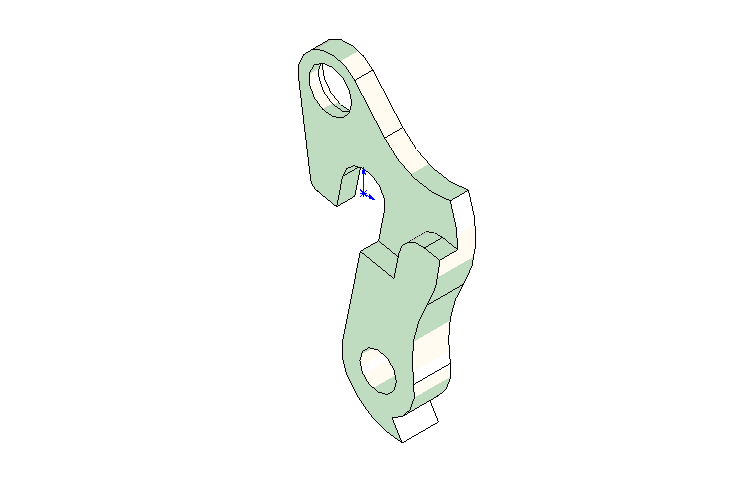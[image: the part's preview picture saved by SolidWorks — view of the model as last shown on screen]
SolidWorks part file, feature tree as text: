
SOLIDWORKS PART (.sldprt)
format: sldprt  version: not decoded by parser v0  size: 365,056 bytes
history: native  units: mm
features: sketch x4, plane x3, cut_extrude x3, material x1, extrude x1 (+10 scaffold rows collapsed)
feature tree (22):
  scaffold x10  (default folders/planes/origin — collapsed)
  material  "Matériau <non spécifié>"
  plane  "Plan de face"
  plane  "Plan de dessus"
  plane  "Plan de droite"
  sketch  "Esquisse33"  dims[c1.D1=22.0mm c1.D2=5.0mm c1.D6=7.5mm c1.D10=~4.910123mm c1.D11=2.0mm c1.D12=5.0mm c1.D15=15.0mm c1.D16=16.5mm c1.D17=26.0mm c1.D18=26.0mm c2.D15=8.5mm c2.D16=36.0mm c2.D18=30.0mm c2.D19=8.5mm c2.D3=7.0mm c3.D3=~11.559837deg c4.D3=~56.867664mm c5.D3=~11.559837deg c5.D4=~457.097187mm c5.D5=~51.596139mm c5.D6=7.0mm c5.D7=15.0mm c5.D8=11.0mm c5.D9=7.0mm c5.D10=11.0mm c5.D12=8.5mm c5.D13=19.5mm c5.D14=~14.769972mm c6.D14=32.26deg c6.D18=13.0mm c6.D19=5.5mm c6.D20=46.5mm c6.D21=7.5mm c7.D20=29.0mm c7.D19=5.0mm c8.D20=5.0mm c9.D20=~23.245536deg c10.D20=42.6mm c10.D16=30.0mm c10.D19=13.0mm c11.D20=4.5mm c12.D20=43.0deg c12.D1=0.0mm]
  extrude  "Extrusion12"  Depth=8.5mm
  sketch  "Esquisse34"  dims[c1.D2=5.0mm c1.D3=8.0mm c1.D4=8.0mm c2.D4=~177.339123deg c3.D4=11.0mm c3.D1=0.0mm]
  cut_extrude  "Enlèv. mat.-Extru.13"  [1 undecoded]
  sketch  "Esquisse35"  dims[D1=10.0mm D2=8.5mm]
  cut_extrude  "Enlèv. mat.-Extru.14"  [1 undecoded]
  sketch  "Esquisse36"  dims[D1=12.3mm]
  cut_extrude  "Enlèv. mat.-Extru.15"  Depth=2mm
decode coverage: 6 of 8 modeling features carry decoded parameters
note: ~ marks probable driven/reference dimensions
note: 2 parameter values undecoded
note: suppression state not decoded; provenance and decode notes live in map.json
